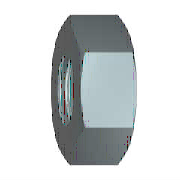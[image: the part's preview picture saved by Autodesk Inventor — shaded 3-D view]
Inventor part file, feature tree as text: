
AUTODESK INVENTOR PART (.ipt)
format: ipt  version: 2021 (Build 250183000, 183)  size: 163,840 bytes
history: native  units: mm (DEFAULTED — no unit token found)
features: sketch x3, chamfer x1, hole x1, other x1, plane x1
ambient origin geometry x7: Origin, YZ Plane, XZ Plane, X Axis, Y Axis, Z Axis, Center Point
bodies: Solid1 (feature_tree), Body (feature_tree)
feature tree (7):
  chamfer  "Chamfer1"  Angle=30.0deg  [1 undecoded]
  hole  "Thread"  [1 undecoded]
  other  "Work Axis1"
  plane  "Work Plane1"
  sketch  "Sketch1"  dims[d0=18.475209mm]
  sketch  "Sketch2"  dims[d1=8.4mm]
  sketch  "Sketch3"  dims[d2=0.0mm d3=30.0deg d4=30.0deg d5=14.6mm d6=14.6mm d7=90.0deg d25=8.376mm d26=6.0mm d27=4.0mm d28=2.0mm d29=14.3117mm d30=8.0mm d31=20.594885mm d8=0.811899mm d9=30.0deg d10=0.811899mm d11=30.0deg d13=0.0mm d14=0.0mm d39=0.0mm d40=0.811899mm d41=0.811899mm d42=0.0mm]
note: 2 required parameter values undecoded (feature->parameter linkage not recoverable at this tier; creation-order binding heuristic only, values carry confidence <= 0.55)
